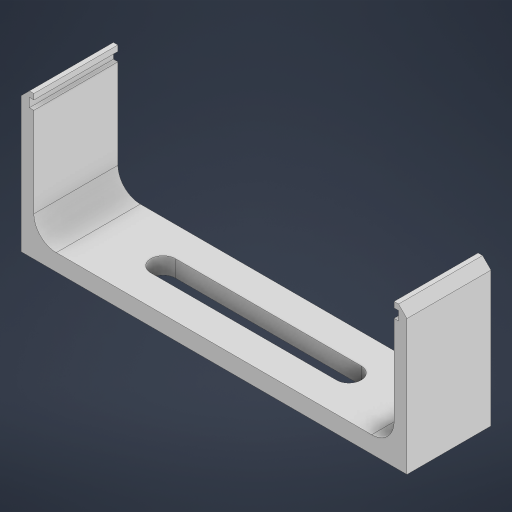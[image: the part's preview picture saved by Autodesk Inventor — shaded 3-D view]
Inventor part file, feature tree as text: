
AUTODESK INVENTOR PART (.ipt)
format: ipt  version: 2023 (Build 270158000, 158)  size: 223,232 bytes
history: native  units: mm
features: extrude x2, sketch x2, mirror x1, chamfer x1, fillet x1, projected_geometry x1
ambient origin geometry x8: Origin, YZ Plane, XZ Plane, XY Plane, X Axis, Y Axis, Z Axis, Center Point
bodies: Solid1 (feature_tree)
feature tree (8):
  extrude  "Extrusion1"  Depth=0.8mm
  mirror  "Mirror1"
  extrude  "Extrusion2"  Depth=1.6mm
  chamfer  "Chamfer1"  Distance=1.5mm
  fillet  "Fillet1"  Radius=20.0mm
  sketch  "Sketch1"  dims[d0=3.0mm d2=0.8mm]
  sketch  "Sketch2"  dims[d3=1.0mm d4=1.6mm d5=1.5mm d9=20.0mm d10=15.0mm d11=0.0mm d12=2.2mm d13=0.0mm d14=0.0mm d15=65.9mm d16=1.5mm d17=2.0mm d18=45.0deg d19=4.0mm]
  projected_geometry  "Projected Loop1"
